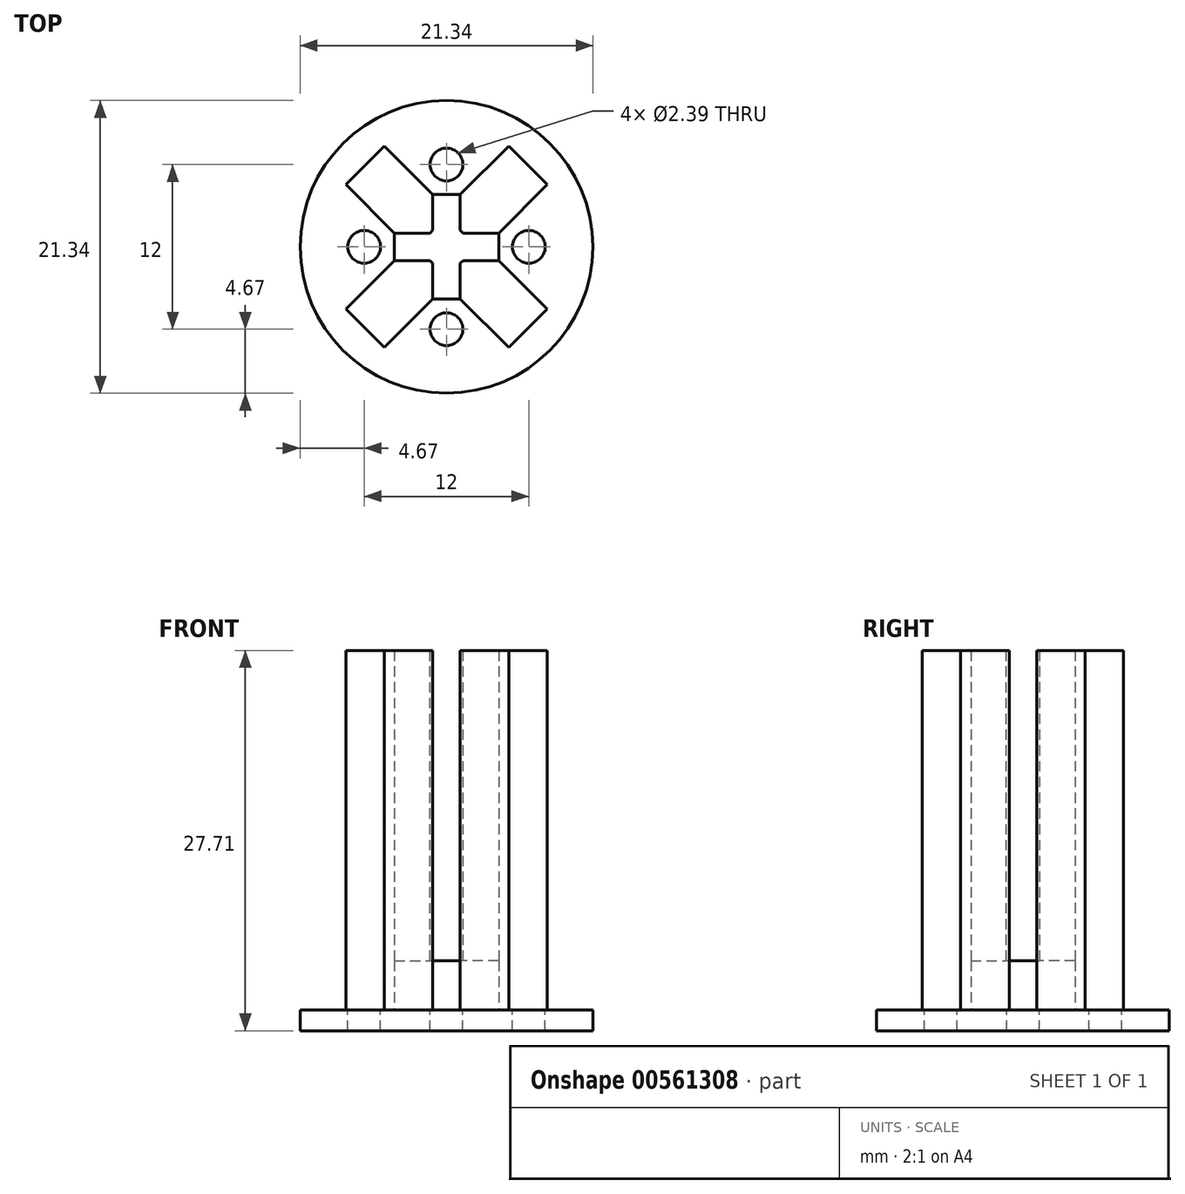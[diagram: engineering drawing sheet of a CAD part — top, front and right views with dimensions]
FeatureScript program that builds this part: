
annotation { "Feature Type Name" : "Feature", "Feature Type Description" : "" }
export const myFeature = defineFeature(function(context is Context, id is Id, definition is map)
    precondition{}
    {
        {
            var Q0;
            Q0=qCreatedBy(makeId("Top.planeOp"),FACE);
            var sketch = newSketch(context, id + "F0", { "sketchPlane" : qUnion([Q0])});
            skCircle(sketch, "E0", {"center": v(0, 0) * mm, "radius": 10.67 * mm});
            skSolve(sketch);
        }
        {
            var Q0;
            Q0 = qSketchRegion(id + "F0", true);
            extrude(context, id + "F1", {"entities" : qUnion([Q0]), "depth" : 1.5 * mm, "offsetDistance" : 25 * mm});
        }
        {
            var Q0;
            Q0=makeQuery(id+"F1.opExtrude","CAP_FACE",FACE,{"disambiguationData":[OSD([sQuery(id+"F0.wireOp",EDGE,"E0")])],"isStart":false});
            var sketch = newSketch(context, id + "F2", { "sketchPlane" : qUnion([Q0])});
            skCircle(sketch, "E1", {"center": v(-6, 0) * mm, "radius": 1.2 * mm});
            skCircle(sketch, "E2", {"center": v(0, 6) * mm, "radius": 1.2 * mm});
            skCircle(sketch, "E3", {"center": v(6, 0) * mm, "radius": 1.2 * mm});
            skCircle(sketch, "E4", {"center": v(0, -6) * mm, "radius": 1.2 * mm});
            skSolve(sketch);
        }
        {
            var Q0;
            Q0 = qSketchRegion(id + "F2", true);
            extrude(context, id + "F3", {"entities" : qUnion([Q0]), "operationType" : NewBodyOperationType.REMOVE, "endBound" : BoundingType.THROUGH_ALL, "oppositeDirection" : true, "depth" : 25 * mm, "offsetDistance" : 25 * mm});
        }
        {
            var Q0;
            Q0=makeQuery(id+"F1.opExtrude","CAP_FACE",FACE,{"disambiguationData":[OSD([sQuery(id+"F0.wireOp",EDGE,"E0")])],"isStart":false});
            var sketch = newSketch(context, id + "F4", { "sketchPlane" : qUnion([Q0])});
            skLineSegment(sketch, "E5.bottom", {"start": v(3.8, 3.8) * mm, "end": v(-3.8, 3.8) * mm});
            skLineSegment(sketch, "E5.top", {"start": v(3.8, -3.8) * mm, "end": v(-3.8, -3.8) * mm});
            skLineSegment(sketch, "E5.left", {"start": v(3.8, 3.8) * mm, "end": v(3.8, -3.8) * mm});
            skLineSegment(sketch, "E5.right", {"start": v(-3.8, 3.8) * mm, "end": v(-3.8, -3.8) * mm});
            skPoint(sketch, "E5.middle", {"position": v(0, 0) * mm});
            skSolve(sketch);
        }
        {
            var Q0;
            Q0=makeQuery(id+"F4.imprint","IMPRINT",FACE,{"disambiguationData":[TD([[makeQuery(id+"F4.imprint","IMPRINT",EDGE,{"derivedFrom":sQuery(id+"F4.wireOp",EDGE,"E5.bottom")}),1.0]])]});
            extrude(context, id + "F5", {"entities" : qUnion([Q0]), "operationType" : NewBodyOperationType.ADD, "depth" : 3.6 * mm, "offsetDistance" : 25 * mm});
        }
        {
            var Q0;
            Q0=makeQuery(id+"F5.opExtrude","CAP_FACE",FACE,{"disambiguationData":[OSD([sQuery(id+"F4.wireOp",EDGE,"E5.bottom"),sQuery(id+"F4.wireOp",EDGE,"E5.top"),sQuery(id+"F4.wireOp",EDGE,"E5.left"),sQuery(id+"F4.wireOp",EDGE,"E5.right")])],"isStart":false});
            var sketch = newSketch(context, id + "F6", { "sketchPlane" : qUnion([Q0])});
            skLineSegment(sketch, "E6.bottom", {"start": v(-3.8, 3.8) * mm, "end": v(-1, 3.8) * mm});
            skLineSegment(sketch, "E6.top", {"start": v(-3.8, 1) * mm, "end": v(-1, 1) * mm});
            skLineSegment(sketch, "E6.left", {"start": v(-3.8, 3.8) * mm, "end": v(-3.8, 1) * mm});
            skLineSegment(sketch, "E6.right", {"start": v(-1, 3.8) * mm, "end": v(-1, 1) * mm});
            skLineSegment(sketch, "E7.bottom", {"start": v(-3.8, -3.8) * mm, "end": v(-1, -3.8) * mm});
            skLineSegment(sketch, "E7.top", {"start": v(-3.8, -1) * mm, "end": v(-1, -1) * mm});
            skLineSegment(sketch, "E7.left", {"start": v(-3.8, -3.8) * mm, "end": v(-3.8, -1) * mm});
            skLineSegment(sketch, "E7.right", {"start": v(-1, -3.8) * mm, "end": v(-1, -1) * mm});
            skLineSegment(sketch, "E8.bottom", {"start": v(3.8, -3.8) * mm, "end": v(1, -3.8) * mm});
            skLineSegment(sketch, "E8.top", {"start": v(3.8, -1) * mm, "end": v(1, -1) * mm});
            skLineSegment(sketch, "E8.left", {"start": v(3.8, -3.8) * mm, "end": v(3.8, -1) * mm});
            skLineSegment(sketch, "E8.right", {"start": v(1, -3.8) * mm, "end": v(1, -1) * mm});
            skLineSegment(sketch, "E9.bottom", {"start": v(3.8, 3.8) * mm, "end": v(1, 3.8) * mm});
            skLineSegment(sketch, "E9.top", {"start": v(3.8, 1) * mm, "end": v(1, 1) * mm});
            skLineSegment(sketch, "E9.left", {"start": v(3.8, 3.8) * mm, "end": v(3.8, 1) * mm});
            skLineSegment(sketch, "E9.right", {"start": v(1, 3.8) * mm, "end": v(1, 1) * mm});
            skSolve(sketch);
        }
        {
            var Q0;
            Q0 = qSketchRegion(id + "F6", true);
            extrude(context, id + "F7", {"entities" : qUnion([Q0]), "operationType" : NewBodyOperationType.ADD, "depth" : 22.6 * mm, "offsetDistance" : 25 * mm});
        }
        {
            var Q0;
            Q0=makeQuery(id+"F1.opExtrude","CAP_FACE",FACE,{"disambiguationData":[OSD([sQuery(id+"F0.wireOp",EDGE,"E0")])],"isStart":false});
            var sketch = newSketch(context, id + "F8", { "sketchPlane" : qUnion([Q0])});
            skLineSegment(sketch, "E10", {"start": v(1, -3.8) * mm, "end": v(4.54, -7.34) * mm});
            skLineSegment(sketch, "E11", {"start": v(4.54, -7.34) * mm, "end": v(7.34, -4.54) * mm});
            skLineSegment(sketch, "E12", {"start": v(7.34, -4.54) * mm, "end": v(3.8, -1) * mm});
            skLineSegment(sketch, "E13", {"start": v(1, -3.8) * mm, "end": v(3.8, -3.8) * mm});
            skLineSegment(sketch, "E14", {"start": v(3.8, -3.8) * mm, "end": v(3.8, -1) * mm});
            skLineSegment(sketch, "E15.1.0", {"start": v(4.54, 7.34) * mm, "end": v(1, 3.8) * mm});
            skLineSegment(sketch, "E15.1.1", {"start": v(7.34, 4.54) * mm, "end": v(4.54, 7.34) * mm});
            skLineSegment(sketch, "E15.1.2", {"start": v(3.8, 1) * mm, "end": v(7.34, 4.54) * mm});
            skLineSegment(sketch, "E15.1.3", {"start": v(3.8, 1) * mm, "end": v(3.8, 3.8) * mm});
            skLineSegment(sketch, "E15.1.4", {"start": v(3.8, 3.8) * mm, "end": v(1, 3.8) * mm});
            skLineSegment(sketch, "E15.2.0", {"start": v(-7.34, 4.54) * mm, "end": v(-3.8, 1) * mm});
            skLineSegment(sketch, "E15.2.1", {"start": v(-4.54, 7.34) * mm, "end": v(-7.34, 4.54) * mm});
            skLineSegment(sketch, "E15.2.2", {"start": v(-1, 3.8) * mm, "end": v(-4.54, 7.34) * mm});
            skLineSegment(sketch, "E15.2.3", {"start": v(-1, 3.8) * mm, "end": v(-3.8, 3.8) * mm});
            skLineSegment(sketch, "E15.2.4", {"start": v(-3.8, 3.8) * mm, "end": v(-3.8, 1) * mm});
            skLineSegment(sketch, "E15.3.0", {"start": v(-4.54, -7.34) * mm, "end": v(-1, -3.8) * mm});
            skLineSegment(sketch, "E15.3.1", {"start": v(-7.34, -4.54) * mm, "end": v(-4.54, -7.34) * mm});
            skLineSegment(sketch, "E15.3.2", {"start": v(-3.8, -1) * mm, "end": v(-7.34, -4.54) * mm});
            skLineSegment(sketch, "E15.3.3", {"start": v(-3.8, -1) * mm, "end": v(-3.8, -3.8) * mm});
            skLineSegment(sketch, "E15.3.4", {"start": v(-3.8, -3.8) * mm, "end": v(-1, -3.8) * mm});
            skPoint(sketch, "E15.center", {"position": v(0, 0) * mm});
            skSolve(sketch);
        }
        {
            var Q0;
            Q0=makeQuery(id+"F8.imprint","IMPRINT",FACE,{"disambiguationData":[TD([[makeQuery(id+"F8.imprint","IMPRINT",EDGE,{"derivedFrom":sQuery(id+"F8.wireOp",EDGE,"E10")}),1.0]])]});
            var Q1;
            Q1=makeQuery(id+"F8.imprint","IMPRINT",FACE,{"disambiguationData":[TD([[makeQuery(id+"F8.imprint","IMPRINT",EDGE,{"derivedFrom":sQuery(id+"F8.wireOp",EDGE,"E15.1.0")}),1.0]])]});
            var Q2;
            Q2=makeQuery(id+"F8.imprint","IMPRINT",FACE,{"disambiguationData":[TD([[makeQuery(id+"F8.imprint","IMPRINT",EDGE,{"derivedFrom":sQuery(id+"F8.wireOp",EDGE,"E15.2.0")}),1.0]])]});
            var Q3;
            Q3=makeQuery(id+"F8.imprint","IMPRINT",FACE,{"disambiguationData":[TD([[makeQuery(id+"F8.imprint","IMPRINT",EDGE,{"derivedFrom":sQuery(id+"F8.wireOp",EDGE,"E15.3.0")}),1.0]])]});
            var Q4;
            Q4=makeQuery(id+"F7.opExtrude","CAP_FACE",FACE,{"disambiguationData":[OSD([sQuery(id+"F6.wireOp",EDGE,"E8.bottom"),sQuery(id+"F6.wireOp",EDGE,"E8.top"),sQuery(id+"F6.wireOp",EDGE,"E8.left"),sQuery(id+"F6.wireOp",EDGE,"E8.right")])],"isStart":false});
            extrude(context, id + "F9", {"entities" : qUnion([Q0, Q1, Q2, Q3]), "operationType" : NewBodyOperationType.ADD, "endBound" : BoundingType.UP_TO_SURFACE, "depth" : 25 * mm, "endBoundEntityFace" : qUnion([Q4]), "offsetDistance" : 25 * mm});
        }
        {
            var Q0;
            Q0=makeQuery(id+"F7.opExtrude","SWEPT_EDGE",EDGE,{"disambiguationData":[OSD([sQuery(id+"F6.wireOp",EDGE,"E6.top"),sQuery(id+"F6.wireOp",EDGE,"E6.right")])]});
            var Q1;
            Q1=makeQuery(id+"F7.opExtrude","SWEPT_EDGE",EDGE,{"disambiguationData":[OSD([sQuery(id+"F6.wireOp",EDGE,"E9.top"),sQuery(id+"F6.wireOp",EDGE,"E9.right")])]});
            var Q2;
            Q2=makeQuery(id+"F7.opExtrude","SWEPT_EDGE",EDGE,{"disambiguationData":[OSD([sQuery(id+"F6.wireOp",EDGE,"E8.top"),sQuery(id+"F6.wireOp",EDGE,"E8.right")])]});
            var Q3;
            Q3=makeQuery(id+"F7.opExtrude","SWEPT_EDGE",EDGE,{"disambiguationData":[OSD([sQuery(id+"F6.wireOp",EDGE,"E7.top"),sQuery(id+"F6.wireOp",EDGE,"E7.right")])]});
            chamfer(context, id + "F10", {"entities" : qUnion([Q0, Q1, Q2, Q3]), "width" : .2 * mm, "tangentPropagation" : true});
        }
    });
